# Revit family: Pro_Filtration_Vandal-Resistant_Connected_Bottle_Filling-Elkay-LVRC8WSPRO_FLP4_FSR5_UV_2FLP4_2FL10
name_source: partatom
category: Plumbing Fixtures
units: mm (PartAtom-declared; Revit-internal decimal feet)

## family parameters
Always vertical = Yes
Cut with Voids When Loaded = No
Maintain Annotation Orientation = No
OmniClass Number = 23.65.70.14.11
OmniClass Title = Drinking Fountains/Coolers
Part Type = Normal
Room Calculation Point = No
Round Connector Dimension = Use Diameter
Shared = No
Work Plane-Based = No

## types (6) — shared parameters
Activation Method = Electronic Bottle Filler Sensor with Mechanical Front Bubbler Button
Assembly Code = D2010810
CW Connection = No
Chilling Capacity (GPH) = 8
Connector Outlet B = 1.25 "
Connector Supply A = 0.375 "
Current = 0 A
Dimensions (L x W x H) = 18 3/8 inch x 19 inch x 46 7/8 inch
Inlet Connection Size (inch) = 0.375 "
Installation Location = Indoor
Main Material = Finish-Elkay-Steel
Manufacturer = Elkay Manufacturer Company
Manufacturer Brand = Elkay (by Zurn Elkay Water Solutions)
Masking Arc Radius = 21 "
Material_Basin = Finish-Elkay-Steel
Material_Bottle Filler = Finish-Elkay-Steel
Material_Bubbler = Finish-Elkay-Steel
Material_Display = Finish-Elkay-Midnight Black
Material_Shroud = Finish-Elkay-Steel
Material_Wrapper = Finish-Elkay-Steel
Number of Poles = 1
Outlet Connection Size (inch) = 1.25 "
Power Factor = 1
Product Documentation Link = https://www.elkayfiles.com
Product Installation Sheet URL = https://www.elkayfiles.com
Product Page URL = https://www.elkay.com
Product data URL = https://www.bimobject.com
Repair Parts URL = https://www.elkayfiles.com
URL = https://www.elkay.com
Voltage = 115 V
Waste Connection = No
zero-valued in all types: CWFU, Default Elevation, HWFU, WFU

## per-type parameters (varying)
| type | Approx. Shipping Weight (lbs) | Description | Model | Product Weight (lbs) |
| LVRC8WSPRO-FLP4 (Elkay Pro Filtration® Vandal-Resistant Connected  Bottle Filling Station&Sgl ADA Cooler Refrig Total PFAS* + Lead Rd SS) | 84 | Elkay Pro Filtration® Vandal-Resistant Connected  Bottle Filling Station&Sgl ADA Cooler Refrig Total PFAS* + Lead Rd SS | LVRC8WSPRO-FLP4 | 79 |
| LVRC8WSPRO-UV (Elkay Pro Filtration® Vandal-Resistant Connected Bottle Filling Station&Sgl ADA Cooler Refrig Ultra-Capacity Lead+UV Prtc SS) | 84 | Elkay Pro Filtration® Vandal-Resistant Connected Bottle Filling Station&Sgl ADA Cooler Refrig Ultra-Capacity Lead+UV Prtc SS | LVRC8WSPRO-UV | 79 |
| LVRC8WSPRO-FSR5 (Elkay Pro Filtration® Vandal-Resistant Connected Bottle Filling Station&Sgl ADA Cooler Refrig Ultra-Capacity Lead Rd SS) | 84 | Elkay Pro Filtration® Vandal-Resistant Connected Bottle Filling Station&Sgl ADA Cooler Refrig Ultra-Capacity Lead Rd SS | LVRC8WSPRO-FSR5 | 79 |
| LVRC8WSPRO  (Elkay Pro Filtration® Vandal-Resistant Connected Bottle Filling Station&Sgl ADA Cooler Refrig Ultra-Capacity Lead Rd SS) | 84 | Elkay Pro Filtration® Vandal-Resistant Connected Bottle Filling Station&Sgl ADA Cooler Refrig Ultra-Capacity Lead Rd SS | LVRC8WSPRO | 79 |
| LVRC8WSPRO-2FLP4 (Elkay Pro Filtration® Vandal-Resistant Connected Bottle Filling Station&Sgl ADA Cooler Refrig Dbl Total  PFAS*+Lead Rd SS) | 86 | Elkay Pro Filtration® Vandal-Resistant Connected Bottle Filling Station&Sgl ADA Cooler Refrig Dbl Total  PFAS*+Lead Rd SS | LVRC8WSPRO-2FLP4 | 81 |
| LVRC8WSPRO-2FL10 (Elkay Pro Filtration® Vandal-Resistant Connected Bottle Filling Station&Sgl ADA Cooler Refrig Ultra-Capacity Lead Rd SS) | 86 | Elkay Pro Filtration® Vandal-Resistant Connected Bottle Filling Station&Sgl ADA Cooler Refrig Ultra-Capacity Lead Rd SS | LVRC8WSPRO-2FL10 | 81 |

## geometry (parser evidence)
native form markers: Sweep x10
no freeform markers — native parametric forms only
